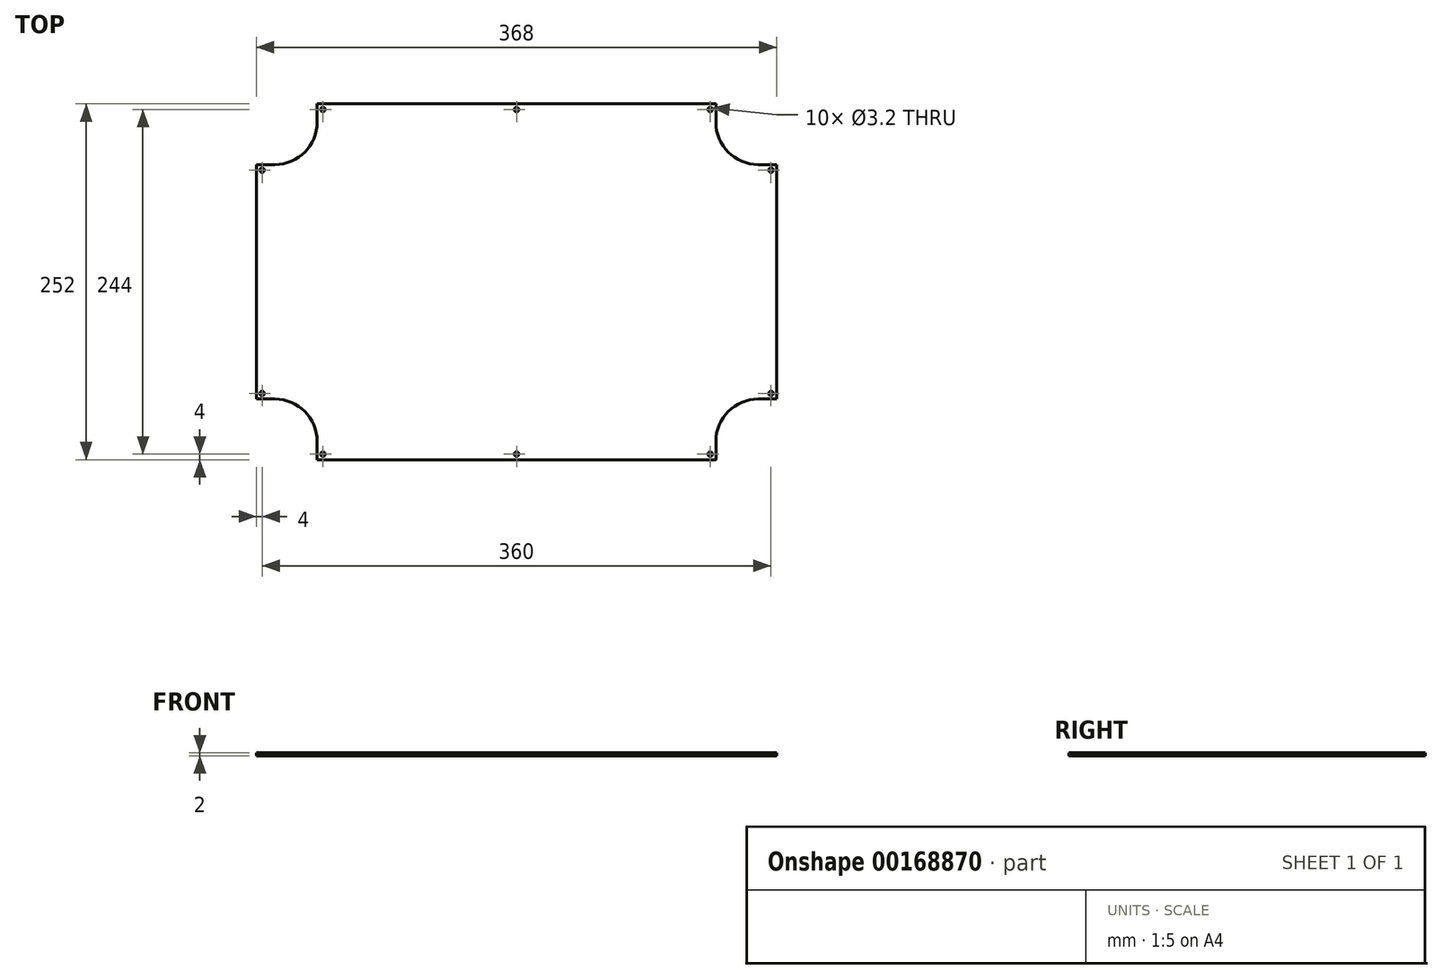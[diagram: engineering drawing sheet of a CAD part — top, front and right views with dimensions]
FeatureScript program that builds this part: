
annotation { "Feature Type Name" : "Feature", "Feature Type Description" : "" }
export const myFeature = defineFeature(function(context is Context, id is Id, definition is map)
    precondition{}
    {
        {
            var Q0;
            Q0=qCreatedBy(makeId("Top.planeOp"),FACE);
            var sketch = newSketch(context, id + "F0", { "sketchPlane" : qUnion([Q0])});
            skLineSegment(sketch, "E0", {"start": v(-141, 126) * mm, "end": v(141, 126) * mm});
            skLineSegment(sketch, "E1", {"start": v(141, 126) * mm, "end": v(141, 113) * mm});
            skLineSegment(sketch, "E2", {"start": v(171, 83) * mm, "end": v(184, 83) * mm});
            skLineSegment(sketch, "E3", {"start": v(184, 83) * mm, "end": v(184, -83) * mm});
            skLineSegment(sketch, "E4", {"start": v(184, -83) * mm, "end": v(171, -83) * mm});
            skLineSegment(sketch, "E5", {"start": v(141, -113) * mm, "end": v(141, -126) * mm});
            skLineSegment(sketch, "E6", {"start": v(141, -126) * mm, "end": v(-141, -126) * mm});
            skLineSegment(sketch, "E7", {"start": v(-141, -126) * mm, "end": v(-141, -113) * mm});
            skLineSegment(sketch, "E8", {"start": v(-171, -83) * mm, "end": v(-184, -83) * mm});
            skLineSegment(sketch, "E9", {"start": v(-184, -83) * mm, "end": v(-184, 83) * mm});
            skLineSegment(sketch, "E10", {"start": v(-184, 83) * mm, "end": v(-171, 83) * mm});
            skLineSegment(sketch, "E11", {"start": v(-141, 113) * mm, "end": v(-141, 126) * mm});
            skPoint(sketch, "E12.visualSharp", {"position": v(-141, 83) * mm});
            skArc(sketch, "E12.filletArc", {"start": v(-171, 83) * mm, "mid": v(-149.79, 91.79) * mm, "end": v(-141, 113) * mm});
            skPoint(sketch, "E13.visualSharp", {"position": v(141, 83) * mm});
            skArc(sketch, "E13.filletArc", {"start": v(141, 113) * mm, "mid": v(149.79, 91.79) * mm, "end": v(171, 83) * mm});
            skPoint(sketch, "E14.visualSharp", {"position": v(141, -83) * mm});
            skArc(sketch, "E14.filletArc", {"start": v(171, -83) * mm, "mid": v(149.79, -91.79) * mm, "end": v(141, -113) * mm});
            skPoint(sketch, "E15.visualSharp", {"position": v(-141, -83) * mm});
            skArc(sketch, "E15.filletArc", {"start": v(-141, -113) * mm, "mid": v(-149.79, -91.79) * mm, "end": v(-171, -83) * mm});
            skPoint(sketch, "E16", {"position": v(0, 126) * mm});
            skPoint(sketch, "E17", {"position": v(0, -126) * mm});
            skPoint(sketch, "E18", {"position": v(-184, 0) * mm});
            skPoint(sketch, "E19", {"position": v(184, 0) * mm});
            skLineSegment(sketch, "E20", {"start": v(-137, 139.15) * mm, "end": v(-137, -174.05) * mm, "construction": true});
            skLineSegment(sketch, "E21", {"start": v(-207.28, 122) * mm, "end": v(169.12, 122) * mm, "construction": true});
            skLineSegment(sketch, "E22", {"start": v(-202.37, 79) * mm, "end": v(209.85, 79) * mm, "construction": true});
            skLineSegment(sketch, "E23.MirrorCS", {"start": v(-202.37, -79) * mm, "end": v(209.85, -79) * mm, "construction": true});
            skLineSegment(sketch, "E24.MirrorCS", {"start": v(-207.28, -122) * mm, "end": v(169.12, -122) * mm, "construction": true});
            skLineSegment(sketch, "E25.MirrorCS", {"start": v(137, 139.15) * mm, "end": v(137, -174.05) * mm, "construction": true});
            skLineSegment(sketch, "E26", {"start": v(-180, 93.5) * mm, "end": v(-180, -106.64) * mm, "construction": true});
            skLineSegment(sketch, "E27.MirrorCS", {"start": v(180, 93.5) * mm, "end": v(180, -106.64) * mm, "construction": true});
            skLineSegment(sketch, "E28", {"start": v(0, 134.08) * mm, "end": v(0, -140) * mm, "construction": true});
            skCircle(sketch, "E29", {"center": v(0, 122) * mm, "radius": 1.6 * mm});
            skCircle(sketch, "E30", {"center": v(-137, 122) * mm, "radius": 1.6 * mm});
            skCircle(sketch, "E31", {"center": v(137, 122) * mm, "radius": 1.6 * mm});
            skCircle(sketch, "E32", {"center": v(-180, 79) * mm, "radius": 1.6 * mm});
            skCircle(sketch, "E33", {"center": v(-180, -79) * mm, "radius": 1.6 * mm});
            skCircle(sketch, "E34", {"center": v(-137, -122) * mm, "radius": 1.6 * mm});
            skCircle(sketch, "E35", {"center": v(0, -122) * mm, "radius": 1.6 * mm});
            skCircle(sketch, "E36", {"center": v(137, -122) * mm, "radius": 1.6 * mm});
            skCircle(sketch, "E37", {"center": v(180, -79) * mm, "radius": 1.6 * mm});
            skCircle(sketch, "E38", {"center": v(180, 79) * mm, "radius": 1.6 * mm});
            skSolve(sketch);
        }
        {
            var Q0;
            Q0=makeQuery(id+"F0.imprint","IMPRINT",FACE,{"disambiguationData":[TD([[makeQuery(id+"F0.imprint","IMPRINT",EDGE,{"derivedFrom":sQuery(id+"F0.wireOp",EDGE,"E0")}),-1.0]])]});
            extrude(context, id + "F1", {"entities" : qUnion([Q0]), "depth" : 2 * mm});
        }
    });
